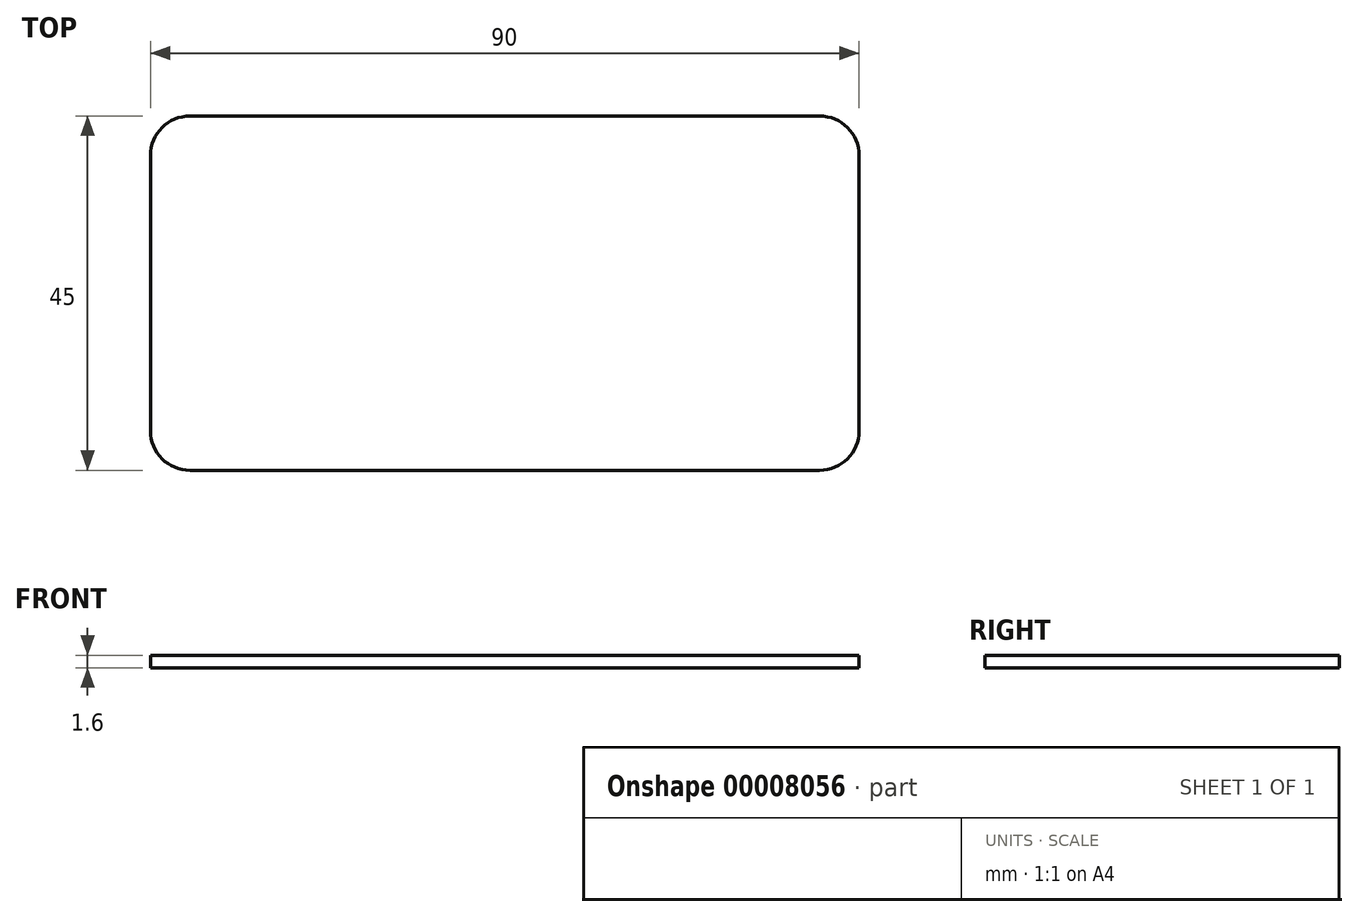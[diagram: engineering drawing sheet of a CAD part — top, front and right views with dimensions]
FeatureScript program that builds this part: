
annotation { "Feature Type Name" : "Feature", "Feature Type Description" : "" }
export const myFeature = defineFeature(function(context is Context, id is Id, definition is map)
    precondition{}
    {
        {
            var Q0;
            Q0=qCreatedBy(makeId("Top.planeOp"),FACE);
            var sketch = newSketch(context, id + "F0", { "sketchPlane" : qUnion([Q0])});
            skLineSegment(sketch, "E0.rect.bottom", {"start": v(40, 22.5) * mm, "end": v(-40, 22.5) * mm});
            skLineSegment(sketch, "E0.rect.top", {"start": v(40, -22.5) * mm, "end": v(-40, -22.5) * mm});
            skLineSegment(sketch, "E0.rect.left", {"start": v(45, 17.5) * mm, "end": v(45, -17.5) * mm});
            skLineSegment(sketch, "E0.rect.right", {"start": v(-45, 17.5) * mm, "end": v(-45, -17.5) * mm});
            skPoint(sketch, "E0.rect.middle", {"position": v(0, 0) * mm});
            skPoint(sketch, "E1.visualSharp", {"position": v(-45, 22.5) * mm});
            skArc(sketch, "E1.filletArc", {"start": v(-40, 22.5) * mm, "mid": v(-43.54, 21.04) * mm, "end": v(-45, 17.5) * mm});
            skPoint(sketch, "E2.visualSharp", {"position": v(45, 22.5) * mm});
            skArc(sketch, "E2.filletArc", {"start": v(45, 17.5) * mm, "mid": v(43.54, 21.04) * mm, "end": v(40, 22.5) * mm});
            skPoint(sketch, "E3.visualSharp", {"position": v(45, -22.5) * mm});
            skArc(sketch, "E3.filletArc", {"start": v(40, -22.5) * mm, "mid": v(43.54, -21.04) * mm, "end": v(45, -17.5) * mm});
            skPoint(sketch, "E4.visualSharp", {"position": v(-45, -22.5) * mm});
            skArc(sketch, "E4.filletArc", {"start": v(-45, -17.5) * mm, "mid": v(-43.54, -21.04) * mm, "end": v(-40, -22.5) * mm});
            skSolve(sketch);
        }
        {
            var Q0;
            Q0 = qSketchRegion(id + "F0", true);
            extrude(context, id + "F1", {"entities" : qUnion([Q0]), "depth" : 1.6 * mm});
        }
    });
